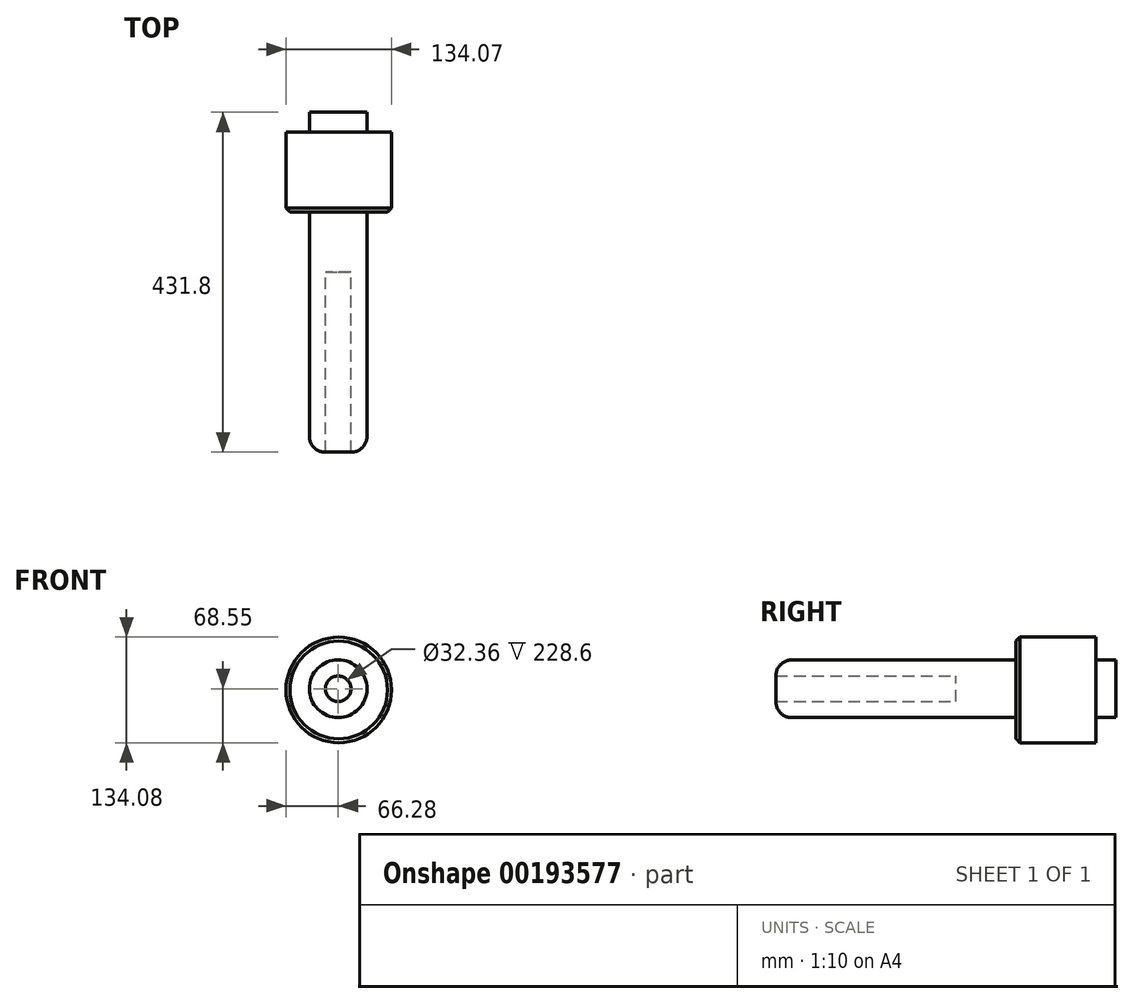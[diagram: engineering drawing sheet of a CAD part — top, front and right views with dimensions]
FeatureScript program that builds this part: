
annotation { "Feature Type Name" : "Feature", "Feature Type Description" : "" }
export const myFeature = defineFeature(function(context is Context, id is Id, definition is map)
    precondition{}
    {
        {
            var Q0;
            Q0=qCreatedBy(makeId("Front.planeOp"),FACE);
            var sketch = newSketch(context, id + "F0", { "sketchPlane" : qUnion([Q0])});
            skCircle(sketch, "E0", {"center": v(0, 0) * mm, "radius": 36.65 * mm});
            skSolve(sketch);
        }
        {
            var Q0;
            Q0=makeQuery(id+"F0.imprint","IMPRINT",FACE,{"disambiguationData":[TD([[makeQuery(id+"F0.imprint","IMPRINT",EDGE,{"derivedFrom":sQuery(id+"F0.wireOp",EDGE,"E0")}),1.0]])]});
            extrude(context, id + "F1", {"entities" : qUnion([Q0]), "depth" : 50.8 * mm});
        }
        {
            var Q0;
            Q0=makeQuery(id+"F1.opExtrude","CAP_FACE",FACE,{"disambiguationData":[OSD([sQuery(id+"F0.wireOp",EDGE,"E0")])],"isStart":false});
            var sketch = newSketch(context, id + "F2", { "sketchPlane" : qUnion([Q0])});
            skCircle(sketch, "E1", {"center": v(0, 0) * mm, "radius": 16.18 * mm});
            skSolve(sketch);
        }
        {
            var Q0;
            Q0=makeQuery(id+"F2.imprint","IMPRINT",FACE,{"disambiguationData":[TD([[makeQuery(id+"F2.imprint","IMPRINT",EDGE,{"derivedFrom":sQuery(id+"F2.wireOp",EDGE,"E1")}),1.0]])]});
            var Q1;
            Q1=sQuery(id+"F2.wireOp",EDGE,"E1");
            extrude(context, id + "F3", {"entities" : qUnion([Q0]), "operationType" : NewBodyOperationType.ADD, "surfaceEntities" : qUnion([Q1]), "depth" : 127 * mm});
        }
        {
            var Q0;
            Q0=makeQuery(id+"F3.opExtrude","CAP_FACE",FACE,{"disambiguationData":[OSD([sQuery(id+"F2.wireOp",EDGE,"E1")])],"isStart":false});
            var sketch = newSketch(context, id + "F4", { "sketchPlane" : qUnion([Q0])});
            skSolve(sketch);
        }
        {
            var Q0;
            Q0=makeQuery(id+"F4.imprint","IMPRINT",FACE,{"disambiguationData":[TD([[makeQuery(id+"F4.imprint","IMPRINT",EDGE,{"derivedFrom":makeQuery(id+"F3.opExtrude","CAP_EDGE",EDGE,{"disambiguationData":[OSD([sQuery(id+"F2.wireOp",EDGE,"E1")])],"isStart":false})}),1.0]])]});
            var sketch = newSketch(context, id + "F5", { "sketchPlane" : qUnion([Q0])});
            skCircle(sketch, "E2", {"center": v(0, 0) * mm, "radius": 28.2 * mm});
            skSolve(sketch);
        }
        {
            var Q0;
            Q0=makeQuery(id+"F5.imprint","IMPRINT",FACE,{"disambiguationData":[TD([[makeQuery(id+"F5.imprint","IMPRINT",EDGE,{"derivedFrom":sQuery(id+"F5.wireOp",EDGE,"E2")}),1.0]])]});
            var Q1;
            Q1=makeQuery(id+"F5.imprint","IMPRINT",FACE,{"disambiguationData":[TD([[makeQuery(id+"F5.imprint","IMPRINT",EDGE,{"derivedFrom":makeQuery(id+"F4.imprint","IMPRINT",EDGE,{"derivedFrom":makeQuery(id+"F3.opExtrude","CAP_EDGE",EDGE,{"disambiguationData":[OSD([sQuery(id+"F2.wireOp",EDGE,"E1")])],"isStart":false})})}),1.0]])]});
            var Q2;
            Q2=makeQuery(id+"F4.imprint","IMPRINT",FACE,{"disambiguationData":[TD([[makeQuery(id+"F4.imprint","IMPRINT",EDGE,{"derivedFrom":makeQuery(id+"F3.opExtrude","CAP_EDGE",EDGE,{"disambiguationData":[OSD([sQuery(id+"F2.wireOp",EDGE,"E1")])],"isStart":false})}),1.0]])]});
            var Q3;
            Q3=makeQuery(id+"F3.opExtrude","CAP_FACE",FACE,{"disambiguationData":[OSD([sQuery(id+"F2.wireOp",EDGE,"E1")])],"isStart":false});
            extrude(context, id + "F6", {"entities" : qUnion([Q0, Q1, Q2, Q3]), "operationType" : NewBodyOperationType.REMOVE, "oppositeDirection" : true, "depth" : 50.8 * mm});
        }
        {
            var Q0;
            Q0=makeQuery(id+"F1.opExtrude","CAP_FACE",FACE,{"disambiguationData":[OSD([sQuery(id+"F0.wireOp",EDGE,"E0")])],"isStart":false});
            var Q1;
            Q1=makeQuery(id+"F1.opExtrude","CAP_FACE",FACE,{"disambiguationData":[OSD([sQuery(id+"F0.wireOp",EDGE,"E0")])],"isStart":true});
            extrude(context, id + "F7", {"entities" : qUnion([Q0, Q1]), "operationType" : NewBodyOperationType.ADD, "depth" : 101.6 * mm});
        }
        {
            var Q0;
            {var subQ0=sQuery(id+"F0.wireOp",EDGE,"E0");Q0=makeQuery(id+"F7.opExtrude","CAP_FACE",FACE,{"disambiguationData":[OSD([subQ0]),TDD([makeQuery(id+"F1.opExtrude","CAP_FACE",FACE,{"disambiguationData":[OSD([subQ0])],"isStart":false})])],"isStart":false});}
            var Q1;
            Q1=makeQuery(id+"F6.boolean.opBoolean","COPY",FACE,{"derivedFrom":makeQuery(id+"F6.opExtrude","CAP_FACE",FACE,{"disambiguationData":[OSD([sQuery(id+"F5.wireOp",EDGE,"E2")])],"isStart":false})});
            var Q2;
            Q2=makeQuery(id+"F1.opExtrude","CAP_FACE",FACE,{"disambiguationData":[OSD([sQuery(id+"F0.wireOp",EDGE,"E0")])],"isStart":true});
            extrude(context, id + "F8", {"entities" : qUnion([Q0, Q1, Q2]), "operationType" : NewBodyOperationType.ADD, "depth" : 50.8 * mm});
        }
        {
            var Q0;
            {var subQ0=sQuery(id+"F0.wireOp",EDGE,"E0");Q0=makeQuery(id+"F8.opExtrude","CAP_FACE",FACE,{"disambiguationData":[OSD([subQ0]),TDD([makeQuery(id+"F7.opExtrude","CAP_FACE",FACE,{"disambiguationData":[OSD([subQ0]),TDD([makeQuery(id+"F1.opExtrude","CAP_FACE",FACE,{"disambiguationData":[OSD([subQ0])],"isStart":false})])],"isStart":false})])],"isStart":false});}
            var Q1;
            Q1=makeQuery(id+"F1.opExtrude","CAP_FACE",FACE,{"disambiguationData":[OSD([sQuery(id+"F0.wireOp",EDGE,"E0")])],"isStart":true});
            extrude(context, id + "F9", {"entities" : qUnion([Q0, Q1]), "operationType" : NewBodyOperationType.ADD, "depth" : 101.6 * mm});
        }
        {
            var Q0;
            Q0=makeQuery(id+"F8.opExtrude","CAP_FACE",FACE,{"disambiguationData":[OSD([sQuery(id+"F5.wireOp",EDGE,"E2")])],"isStart":false});
            var Q1;
            Q1=makeQuery(id+"F1.opExtrude","CAP_FACE",FACE,{"disambiguationData":[OSD([sQuery(id+"F0.wireOp",EDGE,"E0")])],"isStart":true});
            extrude(context, id + "F10", {"entities" : qUnion([Q0, Q1]), "operationType" : NewBodyOperationType.ADD, "oppositeDirection" : true, "depth" : 25.4 * mm});
        }
        {
            var Q0;
            Q0=qCreatedBy(makeId("Front.planeOp"),FACE);
            var sketch = newSketch(context, id + "F11", { "sketchPlane" : qUnion([Q0])});
            skCircle(sketch, "E3", {"center": v(0.76, -1.51) * mm, "radius": 67.04 * mm});
            skSolve(sketch);
        }
        {
            var Q0;
            Q0=makeQuery(id+"F11.imprint","IMPRINT",FACE,{"disambiguationData":[TD([[makeQuery(id+"F11.imprint","IMPRINT",EDGE,{"derivedFrom":sQuery(id+"F11.wireOp",EDGE,"E3")}),1.0]])]});
            var Q1;
            {var subQ0=sQuery(id+"F0.wireOp",EDGE,"E0");Q1=makeQuery(id+"F9.opExtrude","CAP_FACE",FACE,{"disambiguationData":[OSD([subQ0]),TDD([makeQuery(id+"F8.opExtrude","CAP_FACE",FACE,{"disambiguationData":[OSD([subQ0]),TDD([makeQuery(id+"F7.opExtrude","CAP_FACE",FACE,{"disambiguationData":[OSD([subQ0]),TDD([makeQuery(id+"F1.opExtrude","CAP_FACE",FACE,{"disambiguationData":[OSD([subQ0])],"isStart":false})])],"isStart":false})])],"isStart":false})])],"isStart":false});}
            extrude(context, id + "F12", {"entities" : qUnion([Q0, Q1]), "operationType" : NewBodyOperationType.ADD, "depth" : 101.6 * mm});
        }
        {
            var Q0;
            Q0=makeQuery(id+"F12.opExtrude","CAP_EDGE",EDGE,{"disambiguationData":[OSD([sQuery(id+"F0.wireOp",EDGE,"E0")])],"isStart":false});
            fillet(context, id + "F13", {"entities" : qUnion([Q0]), "radius" : 20.32 * mm, "tangentPropagation" : true, "allowEdgeOverflow" : false});
        }
        {
            var Q0;
            Q0=makeQuery(id+"F12.opExtrude","CAP_EDGE",EDGE,{"disambiguationData":[OSD([sQuery(id+"F11.wireOp",EDGE,"E3")])],"isStart":false});
            chamfer(context, id + "F14", {"entities" : qUnion([Q0]), "width" : 5.08 * mm, "tangentPropagation" : true});
        }
    });
